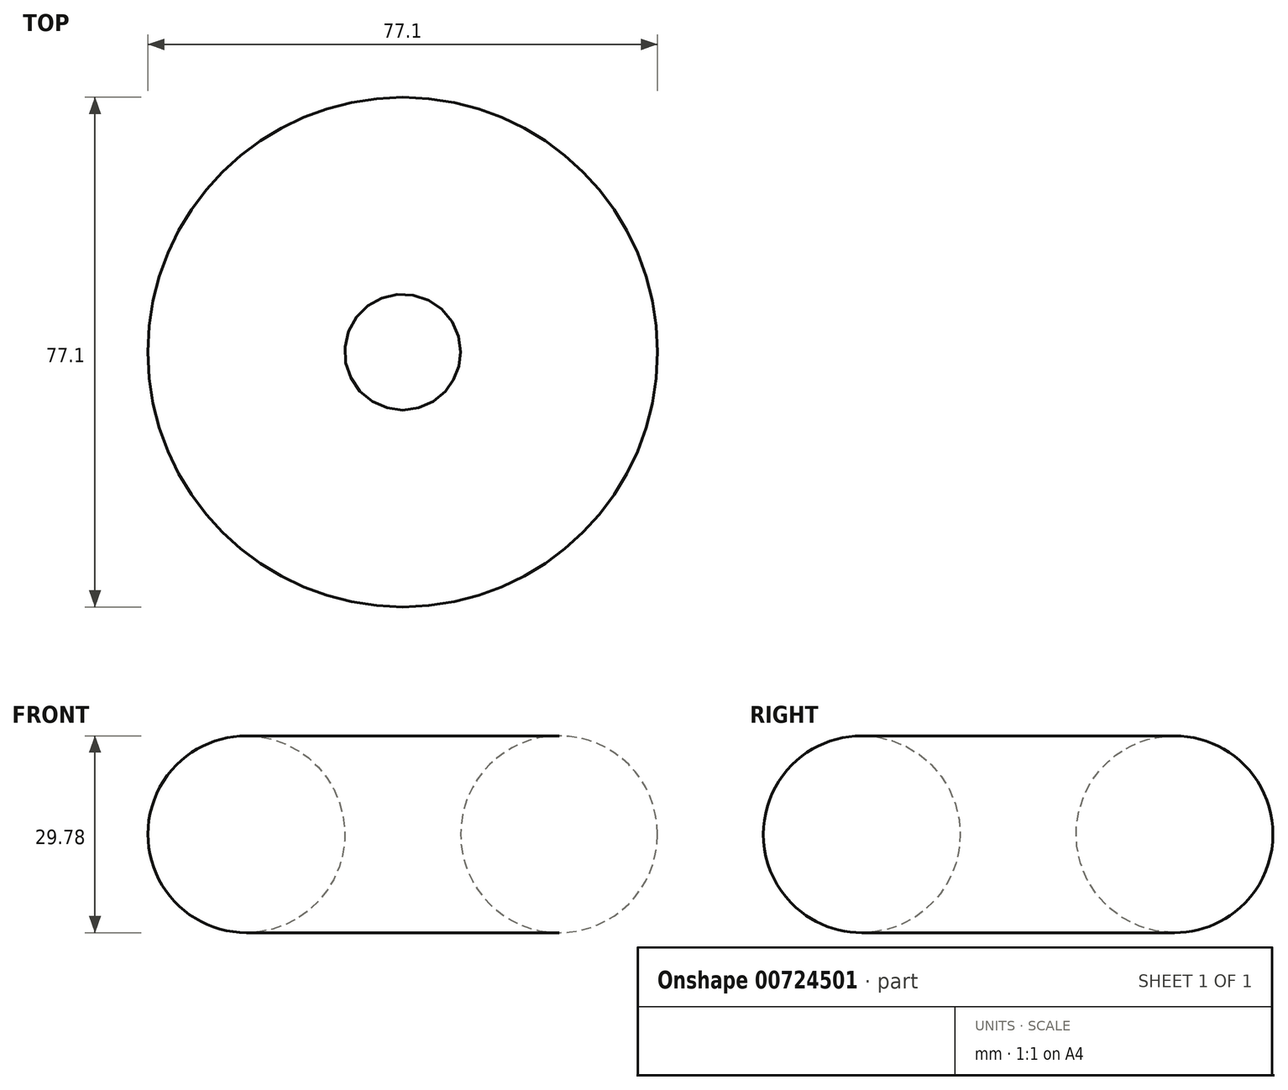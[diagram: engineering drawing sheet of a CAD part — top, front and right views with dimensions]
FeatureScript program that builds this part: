
annotation { "Feature Type Name" : "Feature", "Feature Type Description" : "" }
export const myFeature = defineFeature(function(context is Context, id is Id, definition is map)
    precondition{}
    {
        {
            var Q0;
            Q0=qCreatedBy(makeId("Front.planeOp"),FACE);
            var sketch = newSketch(context, id + "F0", { "sketchPlane" : qUnion([Q0])});
            skCircle(sketch, "E0", {"center": v(23.66, 0) * mm, "radius": 14.9 * mm});
            skLineSegment(sketch, "E1", {"start": v(0, 27.92) * mm, "end": v(0, -26.7) * mm});
            skSolve(sketch);
        }
        {
            var Q0;
            Q0=makeQuery(id+"F0.imprint","IMPRINT",FACE,{"disambiguationData":[TD([[makeQuery(id+"F0.imprint","IMPRINT",EDGE,{"derivedFrom":sQuery(id+"F0.wireOp",EDGE,"E0")}),1.0]])]});
            var Q1;
            Q1=sQuery(id+"F0.wireOp",EDGE,"E1");
            revolve(context, id + "F1", {"surfaceOperationType" : NewSurfaceOperationType.NEW, "entities" : qUnion([Q0]), "axis" : qUnion([Q1]), "revolveType" : RevolveType.FULL});
        }
    });
